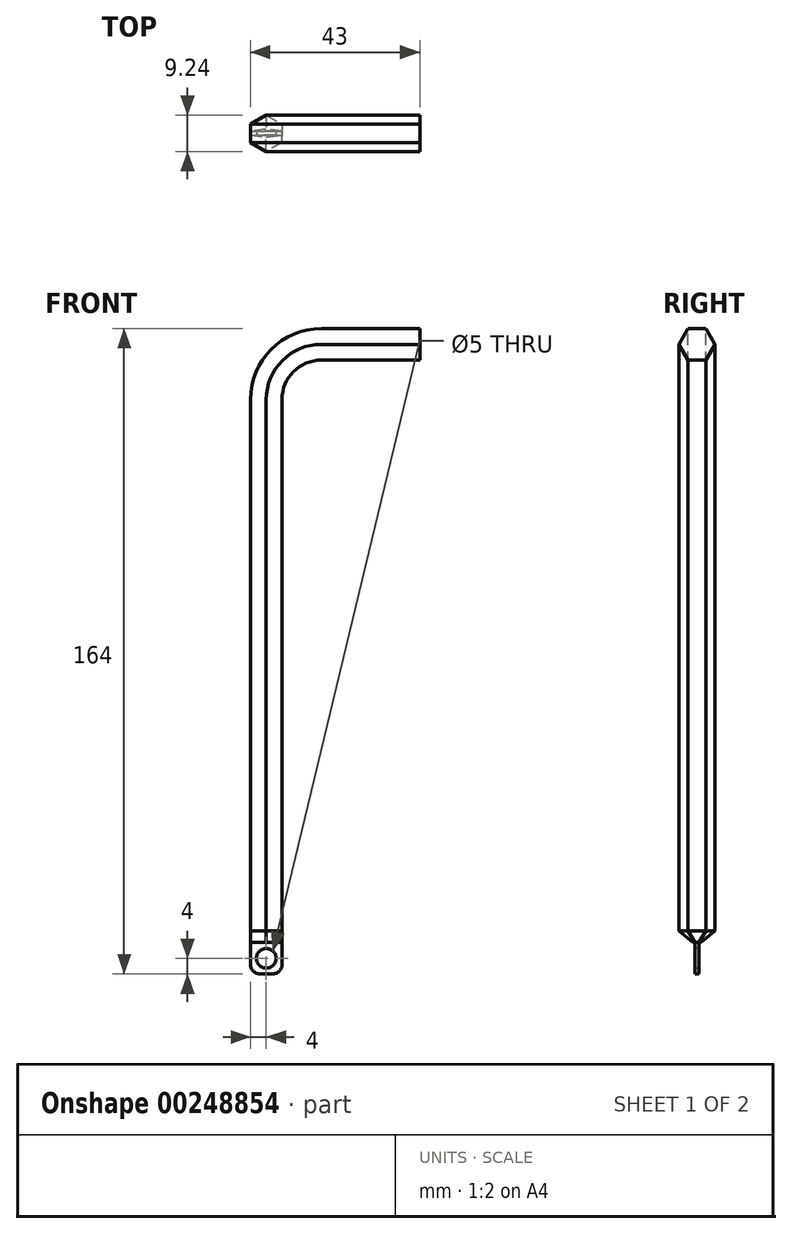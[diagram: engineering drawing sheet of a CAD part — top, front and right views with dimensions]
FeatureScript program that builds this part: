
annotation { "Feature Type Name" : "Feature", "Feature Type Description" : "" }
export const myFeature = defineFeature(function(context is Context, id is Id, definition is map)
    precondition{}
    {
        {
            var Q0;
            Q0=qCreatedBy(makeId("Front.planeOp"),FACE);
            var sketch = newSketch(context, id + "F0", { "sketchPlane" : qUnion([Q0])});
            skLineSegment(sketch, "E0", {"start": v(0, 0) * mm, "end": v(0, 142) * mm});
            skLineSegment(sketch, "E1", {"start": v(14, 156) * mm, "end": v(39, 156) * mm});
            skPoint(sketch, "E2.visualSharp", {"position": v(0, 156) * mm});
            skArc(sketch, "E2.filletArc", {"start": v(14, 156) * mm, "mid": v(4.1, 151.9) * mm, "end": v(0, 142) * mm});
            skLineSegment(sketch, "E3", {"start": v(14, 142) * mm, "end": v(4.1, 151.9) * mm, "construction": true});
            skSolve(sketch);
        }
        {
            var Q0;
            Q0=qCreatedBy(makeId("Top.planeOp"),FACE);
            var sketch = newSketch(context, id + "F1", { "sketchPlane" : qUnion([Q0])});
            skCircle(sketch, "E4.cCircle", {"center": v(0, 0) * mm, "radius": 4 * mm, "construction": true});
            skLineSegment(sketch, "E4.0", {"start": v(-4, 2.3) * mm, "end": v(0, 4.62) * mm});
            skLineSegment(sketch, "E4.1", {"start": v(0, 4.62) * mm, "end": v(4, 2.3) * mm});
            skLineSegment(sketch, "E4.2", {"start": v(4, 2.3) * mm, "end": v(4, -2.3) * mm});
            skLineSegment(sketch, "E4.3", {"start": v(4, -2.3) * mm, "end": v(0, -4.62) * mm});
            skLineSegment(sketch, "E4.4", {"start": v(0, -4.62) * mm, "end": v(-4, -2.3) * mm});
            skLineSegment(sketch, "E4.5", {"start": v(-4, -2.3) * mm, "end": v(-4, 2.3) * mm});
            skSolve(sketch);
        }
        {
            var Q0;
            Q0=qSketchRegion(id+"F1",true);
            var Q1;
            Q1=qConstructionFilter(qBodyType(qCreatedBy(id+"F0",EDGE),BodyType.WIRE),ConstructionObject.NO);
            sweep(context, id + "F2", {"profiles" : qUnion([Q0]), "path" : qUnion([Q1])});
        }
        {
            var Q0;
            Q0=makeQuery(id+"F2.opSweep","CAP_FACE",FACE,{"disambiguationData":[OSD([sQuery(id+"F0.wireOp",VERTEX,"E0.start"),sQuery(id+"F1.wireOp",EDGE,"E4.0"),sQuery(id+"F1.wireOp",EDGE,"E4.1"),sQuery(id+"F1.wireOp",EDGE,"E4.2"),sQuery(id+"F1.wireOp",EDGE,"E4.3"),sQuery(id+"F1.wireOp",EDGE,"E4.4"),sQuery(id+"F1.wireOp",EDGE,"E4.5")])],"isStart":true});
            extrude(context, id + "F3", {"entities" : qUnion([Q0]), "operationType" : NewBodyOperationType.REMOVE, "oppositeDirection" : true, "depth" : 7 * mm});
        }
        {
            var Q0;
            Q0=makeQuery(id+"F3.boolean.opBoolean","COPY",FACE,{"derivedFrom":makeQuery(id+"F3.opExtrude","CAP_FACE",FACE,{"disambiguationData":[OSD([sQuery(id+"F0.wireOp",VERTEX,"E0.start"),sQuery(id+"F1.wireOp",EDGE,"E4.0"),sQuery(id+"F1.wireOp",EDGE,"E4.1"),sQuery(id+"F1.wireOp",EDGE,"E4.2"),sQuery(id+"F1.wireOp",EDGE,"E4.3"),sQuery(id+"F1.wireOp",EDGE,"E4.4"),sQuery(id+"F1.wireOp",EDGE,"E4.5")])],"isStart":false})});
            cPlane(context, id + "F4", {"entities" : qUnion([Q0]), "cplaneType" : CPlaneType.OFFSET, "offset" : 3 * mm, "width" : 150 * mm, "height" : 150 * mm});
        }
        {
            var Q0;
            Q0=qCreatedBy(id+"F4.planeOp",FACE);
            var sketch = newSketch(context, id + "F5", { "sketchPlane" : qUnion([Q0])});
            skLineSegment(sketch, "E5.bottom", {"start": v(-4, 0.5) * mm, "end": v(4, 0.5) * mm});
            skLineSegment(sketch, "E5.top", {"start": v(-4, -0.5) * mm, "end": v(4, -0.5) * mm});
            skLineSegment(sketch, "E5.left", {"start": v(-4, 0.5) * mm, "end": v(-4, -0.5) * mm});
            skLineSegment(sketch, "E5.right", {"start": v(4, 0.5) * mm, "end": v(4, -0.5) * mm});
            skSolve(sketch);
        }
        {
            var Q0;
            Q0 = qSketchRegion(id + "F5", true);
            extrude(context, id + "F6", {"entities" : qUnion([Q0]), "depth" : 8 * mm});
        }
        {
            var Q0;
            Q0=makeQuery(id+"F6.opExtrude","CAP_FACE",FACE,{"disambiguationData":[OSD([sQuery(id+"F5.wireOp",EDGE,"E5.bottom"),sQuery(id+"F5.wireOp",EDGE,"E5.top"),sQuery(id+"F5.wireOp",EDGE,"E5.left"),sQuery(id+"F5.wireOp",EDGE,"E5.right")])],"isStart":true});
            var sketch = newSketch(context, id + "F7", { "sketchPlane" : qUnion([Q0])});
            skPoint(sketch, "E6", {"position": v(0, -0.5) * mm});
            skPoint(sketch, "E7", {"position": v(0, 0.5) * mm});
            skLineSegment(sketch, "E8", {"start": v(-4, 0.5) * mm, "end": v(-4, -0.5) * mm});
            skLineSegment(sketch, "E9", {"start": v(-4, -0.5) * mm, "end": v(0, -1) * mm});
            skLineSegment(sketch, "E10", {"start": v(0, -1) * mm, "end": v(4, -0.5) * mm});
            skLineSegment(sketch, "E11", {"start": v(4, -0.5) * mm, "end": v(4, 0.5) * mm});
            skLineSegment(sketch, "E12", {"start": v(4, 0.5) * mm, "end": v(0, 1) * mm});
            skLineSegment(sketch, "E13", {"start": v(0, 1) * mm, "end": v(-4, 0.5) * mm});
            skSolve(sketch);
        }
        {
            var Q0;
            Q0=makeQuery(id+"F3.boolean.opBoolean","COPY",FACE,{"derivedFrom":makeQuery(id+"F3.opExtrude","CAP_FACE",FACE,{"disambiguationData":[OSD([sQuery(id+"F0.wireOp",VERTEX,"E0.start"),sQuery(id+"F1.wireOp",EDGE,"E4.0"),sQuery(id+"F1.wireOp",EDGE,"E4.1"),sQuery(id+"F1.wireOp",EDGE,"E4.2"),sQuery(id+"F1.wireOp",EDGE,"E4.3"),sQuery(id+"F1.wireOp",EDGE,"E4.4"),sQuery(id+"F1.wireOp",EDGE,"E4.5")])],"isStart":false})});
            var Q1;
            Q1 = qSketchRegion(id + "F7", true);
            loft(context, id + "F8", {"sheetProfilesArray" : [{ "sheetProfileEntities" : qUnion([Q0]) }, { "sheetProfileEntities" : qUnion([Q1]) }]});
        }
        {
            var Q0;
            Q0=makeQuery(id+"F6.opExtrude","SWEPT_FACE",FACE,{"disambiguationData":[OSD([sQuery(id+"F5.wireOp",EDGE,"E5.bottom")])]});
            var sketch = newSketch(context, id + "F9", { "sketchPlane" : qUnion([Q0])});
            skCircle(sketch, "E14", {"center": v(0, 0) * mm, "radius": 2.5 * mm});
            skSolve(sketch);
        }
        {
            var Q0;
            Q0 = qSketchRegion(id + "F9", true);
            extrude(context, id + "F10", {"entities" : qUnion([Q0]), "operationType" : NewBodyOperationType.REMOVE, "oppositeDirection" : true, "depth" : 25 * mm});
        }
        {
            var Q0;
            Q0=makeQuery(id+"F6.opExtrude","CAP_EDGE",EDGE,{"disambiguationData":[OSD([sQuery(id+"F5.wireOp",EDGE,"E5.right")])],"isStart":false});
            var Q1;
            Q1=makeQuery(id+"F6.opExtrude","CAP_EDGE",EDGE,{"disambiguationData":[OSD([sQuery(id+"F5.wireOp",EDGE,"E5.left")])],"isStart":false});
            fillet(context, id + "F11", {"entities" : qUnion([Q0, Q1]), "radius" : 2.5 * mm, "tangentPropagation" : true, "allowEdgeOverflow" : false});
        }
    });
